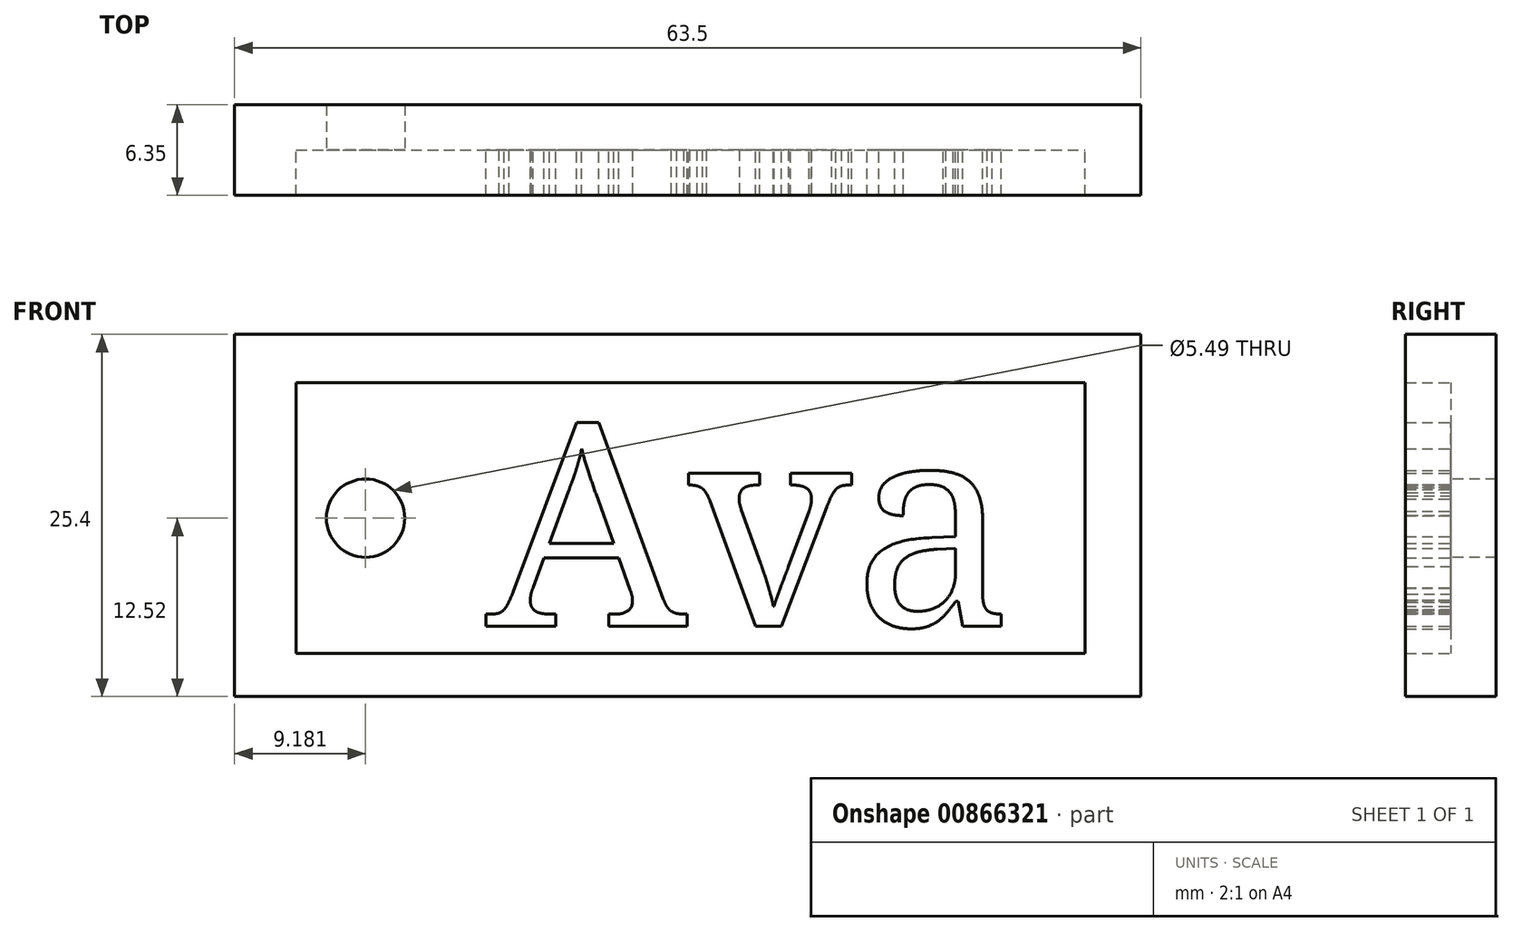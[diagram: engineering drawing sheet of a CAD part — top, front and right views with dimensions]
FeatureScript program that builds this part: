
annotation { "Feature Type Name" : "Feature", "Feature Type Description" : "" }
export const myFeature = defineFeature(function(context is Context, id is Id, definition is map)
    precondition{}
    {
        {
            var Q0;
            Q0=qCreatedBy(makeId("Front.planeOp"),FACE);
            var sketch = newSketch(context, id + "F0", { "sketchPlane" : qUnion([Q0])});
            skLineSegment(sketch, "E0.bottom", {"start": v(0, 25.4) * mm, "end": v(63.5, 25.4) * mm});
            skLineSegment(sketch, "E0.top", {"start": v(0, 0) * mm, "end": v(63.5, 0) * mm});
            skLineSegment(sketch, "E0.left", {"start": v(0, 25.4) * mm, "end": v(0, 0) * mm});
            skLineSegment(sketch, "E0.right", {"start": v(63.5, 25.4) * mm, "end": v(63.5, 0) * mm});
            skLineSegment(sketch, "E1.bottom", {"start": v(4.32, 22.02) * mm, "end": v(59.58, 22.02) * mm});
            skLineSegment(sketch, "E1.top", {"start": v(4.32, 3.02) * mm, "end": v(59.58, 3.02) * mm});
            skLineSegment(sketch, "E1.left", {"start": v(4.32, 22.02) * mm, "end": v(4.32, 3.02) * mm});
            skLineSegment(sketch, "E1.right", {"start": v(59.58, 22.02) * mm, "end": v(59.58, 3.02) * mm});
            skSolve(sketch);
        }
        {
            var Q0;
            Q0 = qSketchRegion(id + "F0", true);
            extrude(context, id + "F1", {"entities" : qUnion([Q0]), "depth" : 6.35 * mm, "offsetDistance" : 25.4 * mm});
        }
        {
            var Q0;
            Q0=makeQuery(id+"F0.imprint","IMPRINT",FACE,{"disambiguationData":[TD([[makeQuery(id+"F0.imprint","IMPRINT",EDGE,{"derivedFrom":sQuery(id+"F0.wireOp",EDGE,"E1.bottom")}),-1.0]])]});
            extrude(context, id + "F2", {"entities" : qUnion([Q0]), "operationType" : NewBodyOperationType.ADD, "depth" : 3.17 * mm, "offsetDistance" : 25.4 * mm});
        }
        {
            var Q0;
            Q0=makeQuery(id+"F2.opExtrude","CAP_FACE",FACE,{"disambiguationData":[OSD([sQuery(id+"F0.wireOp",EDGE,"E1.bottom"),sQuery(id+"F0.wireOp",EDGE,"E1.top"),sQuery(id+"F0.wireOp",EDGE,"E1.left"),sQuery(id+"F0.wireOp",EDGE,"E1.right")])],"isStart":false});
            var sketch = newSketch(context, id + "F3", { "sketchPlane" : qUnion([Q0])});
            skCircle(sketch, "E2", {"center": v(9.18, 12.52) * mm, "radius": 2.74 * mm});
            skPoint(sketch, "E2.centerSnap0", {"position": v(4.32, 12.52) * mm});
            skSolve(sketch);
        }
        {
            var Q0;
            Q0 = qSketchRegion(id + "F3", true);
            extrude(context, id + "F4", {"entities" : qUnion([Q0]), "operationType" : NewBodyOperationType.REMOVE, "oppositeDirection" : true, "depth" : 25.4 * mm, "offsetDistance" : 25.4 * mm});
        }
        {
            var Q0;
            Q0=makeQuery(id+"F2.opExtrude","CAP_FACE",FACE,{"disambiguationData":[OSD([sQuery(id+"F0.wireOp",EDGE,"E1.bottom"),sQuery(id+"F0.wireOp",EDGE,"E1.top"),sQuery(id+"F0.wireOp",EDGE,"E1.left"),sQuery(id+"F0.wireOp",EDGE,"E1.right")])],"isStart":false});
            var sketch = newSketch(context, id + "F5", { "sketchPlane" : qUnion([Q0])});
            skText(sketch, "E3", { "text": "Ava", "fontName": "NotoSerif-Regular.ttf"});
            const initialGuessF5  = {"E3": [0.01762, 0.00495, 1, 0, 0.0144]};
            skSetInitialGuess(sketch, initialGuessF5);
            skSolve(sketch);
        }
        {
            var Q0;
            Q0 = qSketchRegion(id + "F5", true);
            extrude(context, id + "F6", {"entities" : qUnion([Q0]), "operationType" : NewBodyOperationType.ADD, "depth" : 3.17 * mm, "offsetDistance" : 25.4 * mm});
        }
    });
